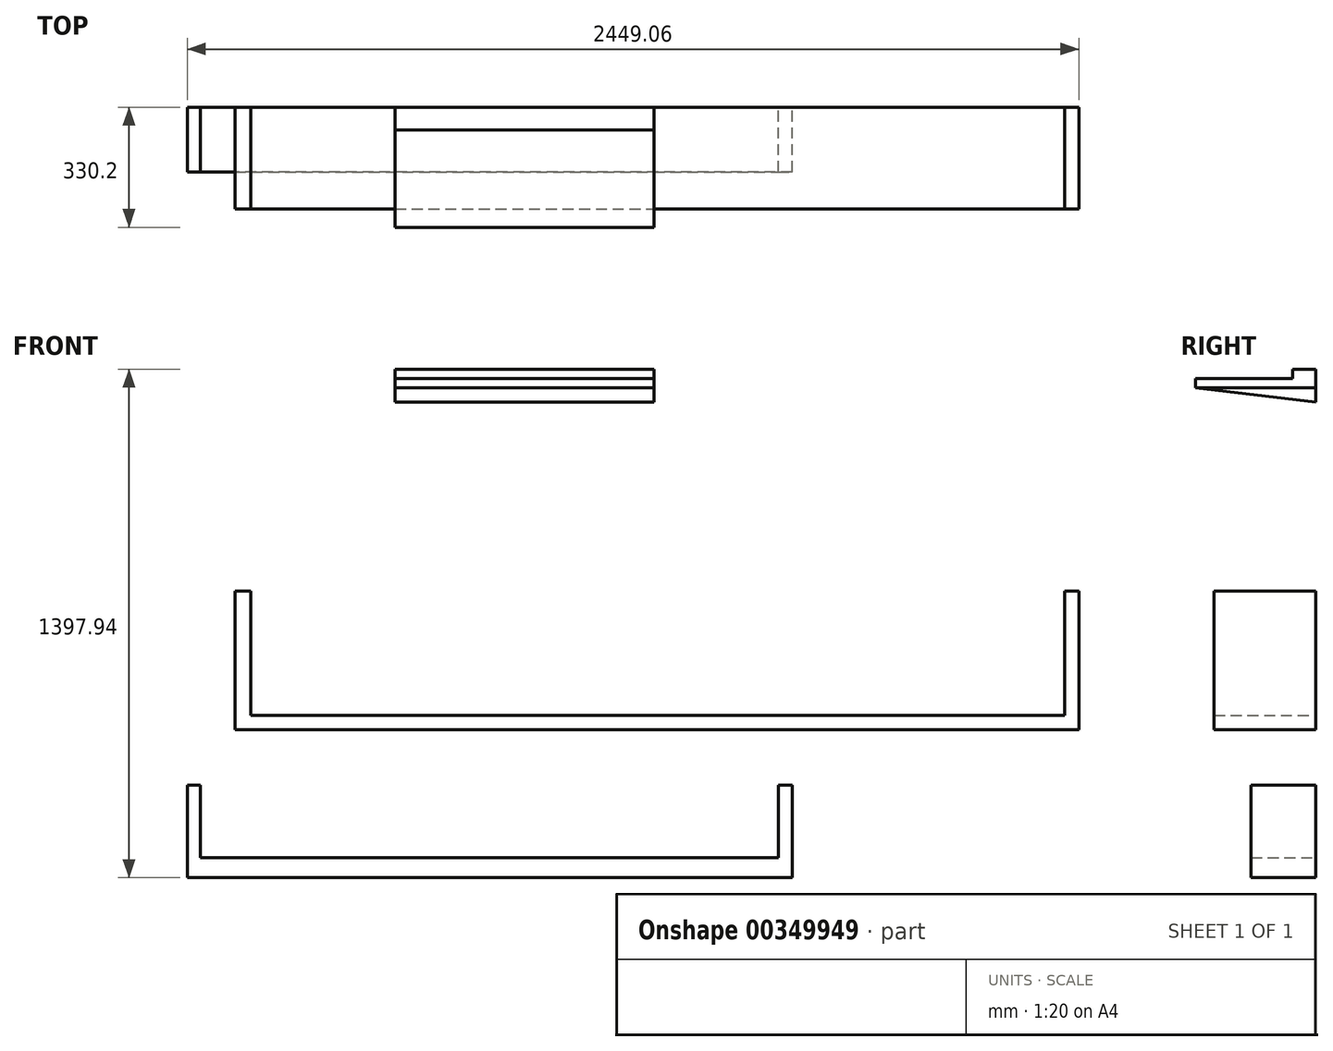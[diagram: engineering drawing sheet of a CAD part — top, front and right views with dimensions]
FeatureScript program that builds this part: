
annotation { "Feature Type Name" : "Feature", "Feature Type Description" : "" }
export const myFeature = defineFeature(function(context is Context, id is Id, definition is map)
    precondition{}
    {
        {
            var Q0;
            Q0=qCreatedBy(makeId("Front.planeOp"),FACE);
            var sketch = newSketch(context, id + "F0", { "sketchPlane" : qUnion([Q0])});
            skLineSegment(sketch, "E0.bottom", {"start": v(-512.78, -284.05) * mm, "end": v(1112.82, -284.05) * mm});
            skLineSegment(sketch, "E0.top", {"start": v(-512.78, -338.75) * mm, "end": v(1112.82, -338.75) * mm});
            skLineSegment(sketch, "E0.left", {"start": v(-512.78, -284.05) * mm, "end": v(-512.78, -338.75) * mm});
            skLineSegment(sketch, "E0.right", {"start": v(1112.82, -284.05) * mm, "end": v(1112.82, -338.75) * mm});
            skLineSegment(sketch, "E1.bottom", {"start": v(-512.78, -338.75) * mm, "end": v(-548.55, -338.75) * mm});
            skLineSegment(sketch, "E1.top", {"start": v(-512.78, -84.75) * mm, "end": v(-548.55, -84.75) * mm});
            skLineSegment(sketch, "E1.left", {"start": v(-512.78, -338.75) * mm, "end": v(-512.78, -84.75) * mm});
            skLineSegment(sketch, "E1.right", {"start": v(-548.55, -338.75) * mm, "end": v(-548.55, -84.75) * mm});
            skLineSegment(sketch, "E2.bottom", {"start": v(1074.72, -338.75) * mm, "end": v(1112.82, -338.75) * mm});
            skLineSegment(sketch, "E2.top", {"start": v(1074.72, -84.75) * mm, "end": v(1112.82, -84.75) * mm});
            skLineSegment(sketch, "E2.left", {"start": v(1112.82, -338.75) * mm, "end": v(1112.82, -84.75) * mm});
            skLineSegment(sketch, "E2.right", {"start": v(1074.72, -338.75) * mm, "end": v(1074.72, -84.75) * mm});
            skSolve(sketch);
        }
        {
            var Q0;
            {var subQ1=sQuery(id+"F0.wireOp",EDGE,"E0.right");var subQ10=sQuery(id+"F0.wireOp",EDGE,"E0.left");var subQ12=makeQuery(id+"F0.imprint","IMPRINT",EDGE,{"derivedFrom":subQ10});var subQ13=sQuery(id+"F0.wireOp",EDGE,"E2.top");Q0=qUnion([makeQuery(id+"F0.imprint","IMPRINT",FACE,{"disambiguationData":[TD([[makeQuery(id+"F0.imprint","IMPRINT",EDGE,{"derivedFrom":subQ13}),-1.0]])]}),makeQuery(id+"F0.imprint","IMPRINT",FACE,{"disambiguationData":[TD([[subQ12,-1.0]])]}),makeQuery(id+"F0.imprint","IMPRINT",FACE,{"disambiguationData":[TD([[subQ12,1.0]])]}),makeQuery(id+"F0.imprint","IMPRINT",FACE,{"disambiguationData":[TD([[makeQuery(id+"F0.imprint","IMPRINT",EDGE,{"derivedFrom":subQ1}),-1.0]])]})]);}
            extrude(context, id + "F1", {"entities" : qUnion([Q0]), "depth" : 177.8 * mm, "offsetDistance" : 25.4 * mm});
        }
        {
            var Q0;
            Q0=qCreatedBy(makeId("Front.planeOp"),FACE);
            var sketch = newSketch(context, id + "F2", { "sketchPlane" : qUnion([Q0])});
            skLineSegment(sketch, "E3.bottom", {"start": v(-373.41, 107.52) * mm, "end": v(1861.79, 107.52) * mm});
            skLineSegment(sketch, "E3.top", {"start": v(-373.41, 68.8) * mm, "end": v(1861.79, 68.8) * mm});
            skLineSegment(sketch, "E3.left", {"start": v(-373.41, 107.52) * mm, "end": v(-373.41, 68.8) * mm});
            skLineSegment(sketch, "E3.right", {"start": v(1861.79, 107.52) * mm, "end": v(1861.79, 68.8) * mm});
            skLineSegment(sketch, "E4.bottom", {"start": v(-373.41, 68.8) * mm, "end": v(-417.67, 68.8) * mm});
            skLineSegment(sketch, "E4.top", {"start": v(-373.41, 449.8) * mm, "end": v(-417.67, 449.8) * mm});
            skLineSegment(sketch, "E4.left", {"start": v(-373.41, 68.8) * mm, "end": v(-373.41, 449.8) * mm});
            skLineSegment(sketch, "E4.right", {"start": v(-417.67, 68.8) * mm, "end": v(-417.67, 449.8) * mm});
            skLineSegment(sketch, "E5.bottom", {"start": v(1861.79, 68.8) * mm, "end": v(1900.51, 68.8) * mm});
            skLineSegment(sketch, "E5.top", {"start": v(1861.79, 449.8) * mm, "end": v(1900.51, 449.8) * mm});
            skLineSegment(sketch, "E5.left", {"start": v(1861.79, 68.8) * mm, "end": v(1861.79, 449.8) * mm});
            skLineSegment(sketch, "E5.right", {"start": v(1900.51, 68.8) * mm, "end": v(1900.51, 449.8) * mm});
            skSolve(sketch);
        }
        {
            var Q0;
            {var subQ0=makeQuery(id+"F2.imprint","IMPRINT",EDGE,{"derivedFrom":sQuery(id+"F2.wireOp",EDGE,"E3.left")});var subQ1=makeQuery(id+"F2.imprint","IMPRINT",EDGE,{"derivedFrom":sQuery(id+"F2.wireOp",EDGE,"E3.right")});Q0=qUnion([makeQuery(id+"F2.imprint","IMPRINT",FACE,{"disambiguationData":[TD([[subQ0,-1.0]])]}),makeQuery(id+"F2.imprint","IMPRINT",FACE,{"disambiguationData":[TD([[subQ1,1.0]])]}),makeQuery(id+"F2.imprint","IMPRINT",FACE,{"disambiguationData":[TD([[makeQuery(id+"F2.imprint","IMPRINT",EDGE,{"derivedFrom":sQuery(id+"F2.wireOp",EDGE,"E3.bottom")}),-1.0]])]})]);}
            extrude(context, id + "F3", {"entities" : qUnion([Q0]), "depth" : 279.4 * mm, "offsetDistance" : 25.4 * mm});
        }
        {
            var Q0;
            Q0=qCreatedBy(makeId("Front.planeOp"),FACE);
            var sketch = newSketch(context, id + "F4", { "sketchPlane" : qUnion([Q0])});
            skLineSegment(sketch, "E6.bottom", {"start": v(22.3, 1033.79) * mm, "end": v(733.68, 1033.79) * mm});
            skLineSegment(sketch, "E6.top", {"start": v(22.3, 1008.39) * mm, "end": v(733.68, 1008.39) * mm});
            skLineSegment(sketch, "E6.left", {"start": v(22.3, 1033.79) * mm, "end": v(22.3, 1008.39) * mm});
            skLineSegment(sketch, "E6.right", {"start": v(733.68, 1033.79) * mm, "end": v(733.68, 1008.39) * mm});
            skSolve(sketch);
        }
        {
            var Q0;
            Q0 = qSketchRegion(id + "F4", true);
            extrude(context, id + "F5", {"entities" : qUnion([Q0]), "depth" : 330.2 * mm, "offsetDistance" : 25.4 * mm});
        }
        {
            var Q0;
            Q0=makeQuery(id+"F5.opExtrude","SWEPT_FACE",FACE,{"disambiguationData":[OSD([sQuery(id+"F4.wireOp",EDGE,"E6.bottom")])]});
            var sketch = newSketch(context, id + "F6", { "sketchPlane" : qUnion([Q0])});
            skLineSegment(sketch, "E7.bottom", {"start": v(733.68, 0) * mm, "end": v(22.3, 0) * mm});
            skLineSegment(sketch, "E7.top", {"start": v(733.68, -62.8) * mm, "end": v(22.3, -62.8) * mm});
            skLineSegment(sketch, "E7.left", {"start": v(733.68, 0) * mm, "end": v(733.68, -62.8) * mm});
            skLineSegment(sketch, "E7.right", {"start": v(22.3, 0) * mm, "end": v(22.3, -62.8) * mm});
            skSolve(sketch);
        }
        {
            var Q0;
            Q0 = qSketchRegion(id + "F6", true);
            extrude(context, id + "F7", {"entities" : qUnion([Q0]), "operationType" : NewBodyOperationType.ADD, "depth" : 25.4 * mm, "offsetDistance" : 25.4 * mm});
        }
        {
            var Q0;
            Q0=makeQuery(id+"F7.boolean.opBoolean","MERGE",FACE,{"derivedFrom":[makeQuery(id+"F5.opExtrude","SWEPT_FACE",FACE,{"disambiguationData":[OSD([sQuery(id+"F4.wireOp",EDGE,"E6.left")])]}),makeQuery(id+"F7.opExtrude","SWEPT_FACE",FACE,{"disambiguationData":[OSD([sQuery(id+"F6.wireOp",EDGE,"E7.right")])]})]});
            var sketch = newSketch(context, id + "F8", { "sketchPlane" : qUnion([Q0])});
            skLineSegment(sketch, "E8", {"start": v(0, 1008.39) * mm, "end": v(330.2, 1008.39) * mm});
            skLineSegment(sketch, "E9", {"start": v(330.2, 1008.39) * mm, "end": v(0, 968.2) * mm});
            skLineSegment(sketch, "E10", {"start": v(0, 968.2) * mm, "end": v(0, 1008.39) * mm});
            skSolve(sketch);
        }
        {
            var Q0;
            Q0 = qSketchRegion(id + "F8", true);
            extrude(context, id + "F9", {"entities" : qUnion([Q0]), "operationType" : NewBodyOperationType.ADD, "oppositeDirection" : true, "depth" : 711.2 * mm, "offsetDistance" : 25.4 * mm});
        }
    });
